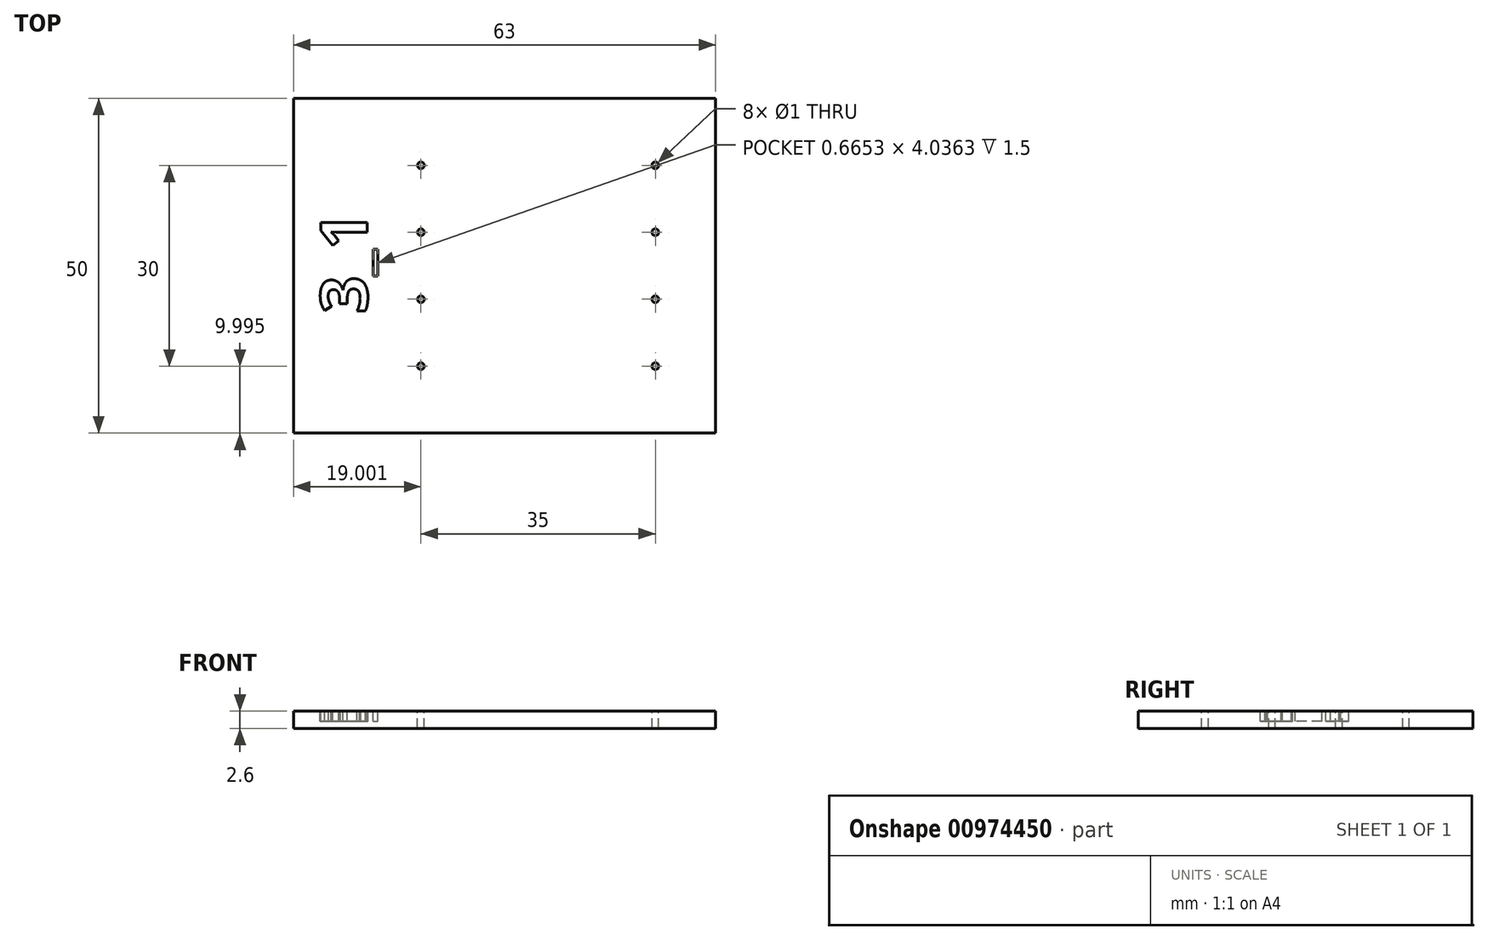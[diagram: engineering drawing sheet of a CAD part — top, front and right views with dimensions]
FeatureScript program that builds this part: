
annotation { "Feature Type Name" : "Feature", "Feature Type Description" : "" }
export const myFeature = defineFeature(function(context is Context, id is Id, definition is map)
    precondition{}
    {
        {
            var Q0;
            Q0=qCreatedBy(makeId("Top.planeOp"),FACE);
            var sketch = newSketch(context, id + "F0", { "sketchPlane" : qUnion([Q0])});
            skLineSegment(sketch, "E0.bottom", {"start": v(-43.16, 28.34) * mm, "end": v(19.84, 28.34) * mm});
            skLineSegment(sketch, "E0.top", {"start": v(-43.16, -21.66) * mm, "end": v(19.84, -21.66) * mm});
            skLineSegment(sketch, "E0.left", {"start": v(-43.16, 28.34) * mm, "end": v(-43.16, -21.66) * mm});
            skLineSegment(sketch, "E0.right", {"start": v(19.84, 28.34) * mm, "end": v(19.84, -21.66) * mm});
            skSolve(sketch);
        }
        {
            var Q0;
            Q0=makeQuery(id+"F0.imprint","IMPRINT",FACE,{"disambiguationData":[TD([[makeQuery(id+"F0.imprint","IMPRINT",EDGE,{"derivedFrom":sQuery(id+"F0.wireOp",EDGE,"E0.bottom")}),-1.0]])]});
            extrude(context, id + "F1", {"entities" : qUnion([Q0]), "depth" : 2.6 * mm, "offsetDistance" : 25 * mm});
        }
        {
            var Q0;
            Q0=makeQuery(id+"F1.opExtrude","CAP_FACE",FACE,{"disambiguationData":[OSD([sQuery(id+"F0.wireOp",EDGE,"E0.bottom"),sQuery(id+"F0.wireOp",EDGE,"E0.top"),sQuery(id+"F0.wireOp",EDGE,"E0.left"),sQuery(id+"F0.wireOp",EDGE,"E0.right")])],"isStart":false});
            var sketch = newSketch(context, id + "F2", { "sketchPlane" : qUnion([Q0])});
            skText(sketch, "E1", { "text": "3_1", "fontName": "OpenSans-Bold.ttf"});
            const initialGuessF2  = {"E1": [-0.03216, -0.00376, 0, 1, 0.007]};
            skSetInitialGuess(sketch, initialGuessF2);
            skSolve(sketch);
        }
        {
            var Q0;
            Q0=qSketchRegion(id+"F2",true);
            extrude(context, id + "F3", {"entities" : qUnion([Q0]), "operationType" : NewBodyOperationType.REMOVE, "oppositeDirection" : true, "depth" : 1.5 * mm, "offsetDistance" : 25 * mm});
        }
        {
            var Q0;
            {var subQ0=sQuery(id+"F0.wireOp",EDGE,"E0.left");var subQ1=sQuery(id+"F0.wireOp",EDGE,"E0.bottom");var subQ2=sQuery(id+"F0.wireOp",EDGE,"E0.right");var subQ3=sQuery(id+"F0.wireOp",EDGE,"E0.top");Q0=makeQuery(id+"F3.boolean.opBoolean","SPLIT",FACE,{"disambiguationData":[TD([makeQuery(id+"F1.opExtrude","SWEPT_FACE",FACE,{"disambiguationData":[OSD([subQ1])]})])],"derivedFrom":makeQuery(id+"F1.opExtrude","CAP_FACE",FACE,{"disambiguationData":[OSD([subQ1,subQ3,subQ0,subQ2])],"isStart":false})});}
            var sketch = newSketch(context, id + "F4", { "sketchPlane" : qUnion([Q0])});
            skCircle(sketch, "E2", {"center": v(-24.16, -11.66) * mm, "radius": 0.5 * mm});
            skCircle(sketch, "E3", {"center": v(-24.16, -1.66) * mm, "radius": 0.5 * mm});
            skCircle(sketch, "E4", {"center": v(-24.16, 8.34) * mm, "radius": 0.5 * mm});
            skCircle(sketch, "E5", {"center": v(-24.16, 18.34) * mm, "radius": 0.5 * mm});
            skCircle(sketch, "E6", {"center": v(10.84, -11.66) * mm, "radius": 0.5 * mm});
            skCircle(sketch, "E7", {"center": v(10.84, -1.66) * mm, "radius": 0.5 * mm});
            skCircle(sketch, "E8", {"center": v(10.84, 8.34) * mm, "radius": 0.5 * mm});
            skCircle(sketch, "E9", {"center": v(10.84, 18.34) * mm, "radius": 0.5 * mm});
            skSolve(sketch);
        }
        {
            var Q0;
            Q0 = qSketchRegion(id + "F4", true);
            extrude(context, id + "F5", {"entities" : qUnion([Q0]), "operationType" : NewBodyOperationType.REMOVE, "endBound" : BoundingType.UP_TO_NEXT, "oppositeDirection" : true, "depth" : 25 * mm, "offsetDistance" : 25 * mm});
        }
    });
